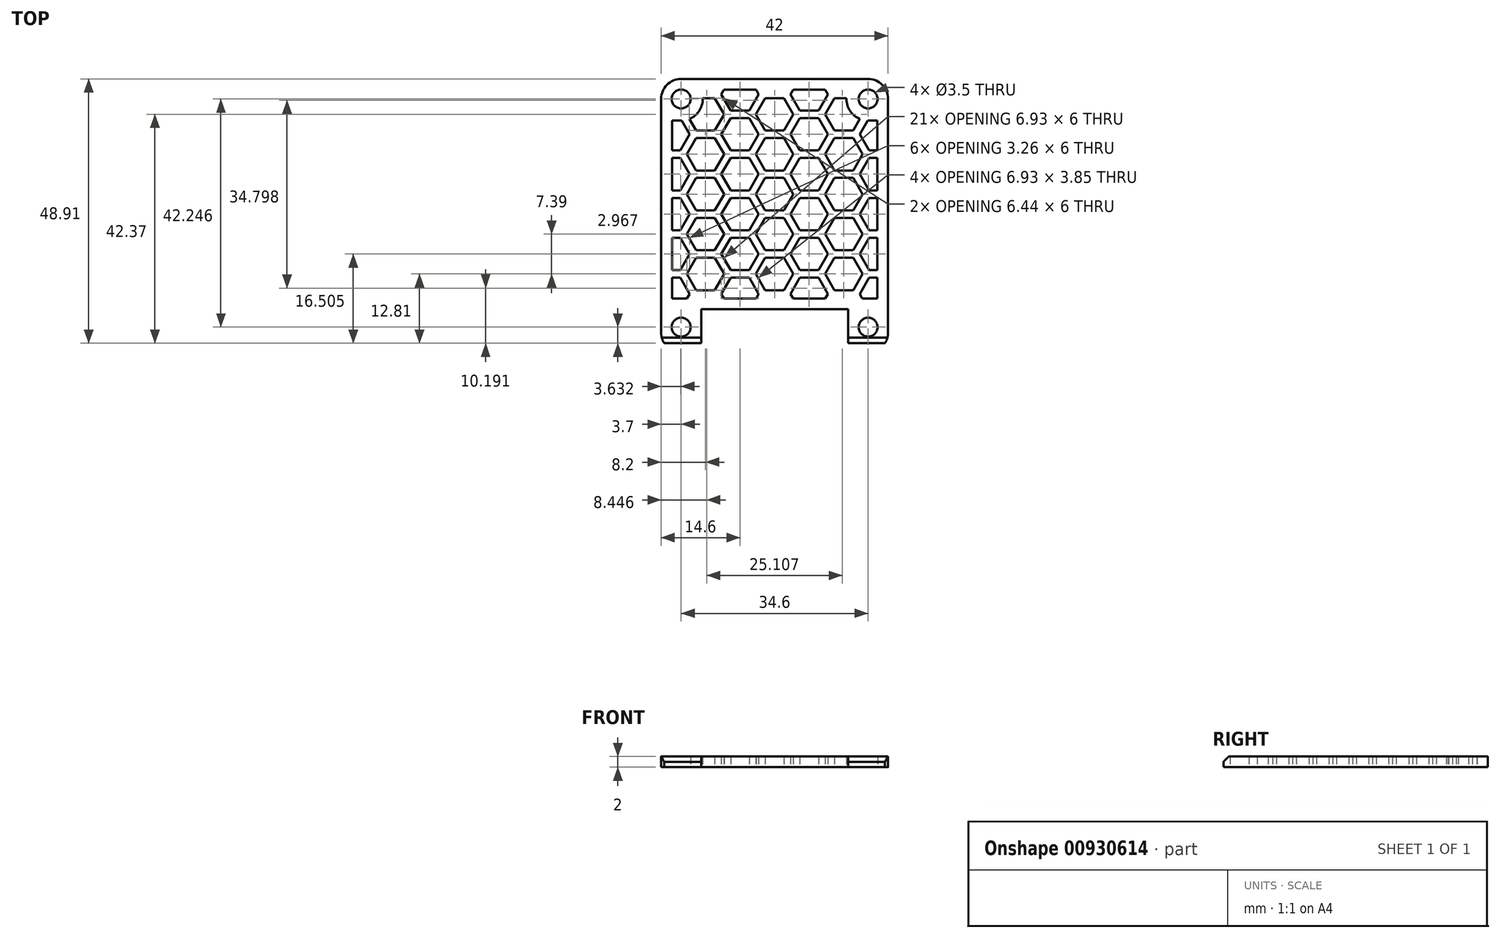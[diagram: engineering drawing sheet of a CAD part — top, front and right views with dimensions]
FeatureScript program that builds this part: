
annotation { "Feature Type Name" : "Feature", "Feature Type Description" : "" }
export const myFeature = defineFeature(function(context is Context, id is Id, definition is map)
    precondition{}
    {
        {
            var Q0;
            Q0=qCreatedBy(makeId("Top.planeOp"),FACE);
            var sketch = newSketch(context, id + "F0", { "sketchPlane" : qUnion([Q0])});
            skLineSegment(sketch, "E0", {"start": v(-21.3, 17.62) * mm, "end": v(-21.3, -25.62) * mm, "construction": true});
            skArc(sketch, "E1", {"start": v(-17.3, 21.62) * mm, "mid": v(-20.13, 20.45) * mm, "end": v(-21.3, 17.62) * mm, "construction": true});
            skLineSegment(sketch, "E2", {"start": v(-17.3, 21.62) * mm, "end": v(17.3, 21.62) * mm, "construction": true});
            skArc(sketch, "E3", {"start": v(21.3, 17.62) * mm, "mid": v(20.13, 20.45) * mm, "end": v(17.3, 21.62) * mm, "construction": true});
            skLineSegment(sketch, "E4", {"start": v(21.3, 17.62) * mm, "end": v(21.3, -25.62) * mm, "construction": true});
            skLineSegment(sketch, "E5", {"start": v(-13.3, -21.62) * mm, "end": v(13.3, -21.62) * mm, "construction": true});
            skLineSegment(sketch, "E6", {"start": v(13.3, -21.62) * mm, "end": v(13.3, -27.6) * mm, "construction": true});
            skLineSegment(sketch, "E7", {"start": v(-13.3, -21.62) * mm, "end": v(-13.3, -27.6) * mm, "construction": true});
            skArc(sketch, "E8", {"start": v(-21.3, -25.62) * mm, "mid": v(-21.17, -26.64) * mm, "end": v(-20.78, -27.6) * mm, "construction": true});
            skLineSegment(sketch, "E9", {"start": v(-20.78, -27.6) * mm, "end": v(-13.3, -27.6) * mm, "construction": true});
            skLineSegment(sketch, "E10", {"start": v(13.3, -27.6) * mm, "end": v(20.78, -27.6) * mm, "construction": true});
            skArc(sketch, "E11", {"start": v(20.78, -27.6) * mm, "mid": v(21.17, -26.64) * mm, "end": v(21.3, -25.62) * mm, "construction": true});
            skCircle(sketch, "E12", {"center": v(-17.3, 17.62) * mm, "radius": 1.4 * mm, "construction": true});
            skCircle(sketch, "E13", {"center": v(17.3, 17.62) * mm, "radius": 1.4 * mm, "construction": true});
            skCircle(sketch, "E14", {"center": v(-17.3, -24.62) * mm, "radius": 1.4 * mm, "construction": true});
            skCircle(sketch, "E15", {"center": v(17.3, -24.62) * mm, "radius": 1.4 * mm, "construction": true});
            skSolve(sketch);
        }
        {
            var Q0;
            Q0=qCreatedBy(makeId("Top.planeOp"),FACE);
            var sketch = newSketch(context, id + "F1", { "sketchPlane" : qUnion([Q0])});
            skLineSegment(sketch, "E16", {"start": v(-21, 17.62) * mm, "end": v(-21, -25.62) * mm});
            skLineSegment(sketch, "E17", {"start": v(-20.43, -27.6) * mm, "end": v(-13.6, -27.6) * mm});
            skLineSegment(sketch, "E18", {"start": v(-13.6, -27.6) * mm, "end": v(-13.6, -21.32) * mm});
            skArc(sketch, "E19", {"start": v(-21, -25.62) * mm, "mid": v(-20.85, -26.65) * mm, "end": v(-20.43, -27.6) * mm});
            skLineSegment(sketch, "E20", {"start": v(-17.3, 21.32) * mm, "end": v(17.3, 21.32) * mm});
            skLineSegment(sketch, "E21", {"start": v(21, 17.62) * mm, "end": v(21, -25.62) * mm});
            skLineSegment(sketch, "E22", {"start": v(-13.6, -21.32) * mm, "end": v(13.6, -21.32) * mm});
            skLineSegment(sketch, "E23", {"start": v(13.6, -21.32) * mm, "end": v(13.6, -27.6) * mm});
            skLineSegment(sketch, "E24", {"start": v(13.6, -27.6) * mm, "end": v(20.43, -27.6) * mm});
            skArc(sketch, "E25", {"start": v(20.43, -27.6) * mm, "mid": v(20.85, -26.65) * mm, "end": v(21, -25.62) * mm});
            skArc(sketch, "E26", {"start": v(21, 17.62) * mm, "mid": v(19.92, 20.24) * mm, "end": v(17.3, 21.32) * mm});
            skArc(sketch, "E27", {"start": v(-17.3, 21.32) * mm, "mid": v(-19.92, 20.24) * mm, "end": v(-21, 17.62) * mm});
            skCircle(sketch, "E28", {"center": v(-17.3, 17.62) * mm, "radius": 1.75 * mm});
            skCircle(sketch, "E29", {"center": v(17.3, 17.62) * mm, "radius": 1.75 * mm});
            skCircle(sketch, "E30", {"center": v(-17.3, -24.62) * mm, "radius": 1.75 * mm});
            skCircle(sketch, "E31", {"center": v(17.3, -24.62) * mm, "radius": 1.75 * mm});
            skLineSegment(sketch, "E32", {"start": v(-9.37, 19.32) * mm, "end": v(-3.43, 19.32) * mm});
            skLineSegment(sketch, "E33", {"start": v(13.3, 17.78) * mm, "end": v(13.3, 17.62) * mm});
            skLineSegment(sketch, "E34", {"start": v(-13.3, 17.78) * mm, "end": v(-13.3, 17.62) * mm});
            skLineSegment(sketch, "E35", {"start": v(-19, -19.32) * mm, "end": v(-16.23, -19.32) * mm});
            skLineSegment(sketch, "E36", {"start": v(19, -19.32) * mm, "end": v(19, -15.48) * mm});
            skLineSegment(sketch, "E37", {"start": v(19, 13.62) * mm, "end": v(17.3, 13.62) * mm});
            skLineSegment(sketch, "E38", {"start": v(-19, -19.32) * mm, "end": v(-19, -15.48) * mm});
            skLineSegment(sketch, "E39", {"start": v(-19, 13.62) * mm, "end": v(-17.3, 13.62) * mm});
            skArc(sketch, "E40", {"start": v(-17.3, 13.62) * mm, "mid": v(-17.25, 13.62) * mm, "end": v(-17.2, 13.62) * mm});
            skArc(sketch, "E41", {"start": v(13.3, 17.62) * mm, "mid": v(13.97, 15.4) * mm, "end": v(15.77, 13.93) * mm});
            skCircle(sketch, "E42.cCircle", {"center": v(0, 0) * mm, "radius": 3 * mm, "construction": true});
            skLineSegment(sketch, "E42.0", {"start": v(1.73, 3) * mm, "end": v(3.46, 0) * mm});
            skLineSegment(sketch, "E42.1", {"start": v(3.46, 0) * mm, "end": v(1.73, -3) * mm});
            skLineSegment(sketch, "E42.2", {"start": v(1.73, -3) * mm, "end": v(-1.73, -3) * mm});
            skLineSegment(sketch, "E42.3", {"start": v(-1.73, -3) * mm, "end": v(-3.46, 0) * mm});
            skLineSegment(sketch, "E42.4", {"start": v(-3.46, 0) * mm, "end": v(-1.73, 3) * mm});
            skLineSegment(sketch, "E42.5", {"start": v(-1.73, 3) * mm, "end": v(1.73, 3) * mm});
            skPoint(sketch, "E42.0.midPoint", {"position": v(2.6, 1.5) * mm});
            skLineSegment(sketch, "E43", {"start": v(-19, 10.97) * mm, "end": v(19, -10.97) * mm, "construction": true});
            skLineSegment(sketch, "E44", {"start": v(-19, -10.97) * mm, "end": v(19, 10.97) * mm, "construction": true});
            skLineSegment(sketch, "E45", {"start": v(-13.95, 15.44) * mm, "end": v(19, -3.58) * mm, "construction": true});
            skCircle(sketch, "E46.cCircle", {"center": v(6.4, 3.7) * mm, "radius": 3 * mm, "construction": true});
            skLineSegment(sketch, "E46.0", {"start": v(8.13, 6.7) * mm, "end": v(9.86, 3.7) * mm});
            skLineSegment(sketch, "E46.1", {"start": v(9.86, 3.7) * mm, "end": v(8.13, 0.7) * mm});
            skLineSegment(sketch, "E46.2", {"start": v(8.13, 0.7) * mm, "end": v(4.67, 0.7) * mm});
            skLineSegment(sketch, "E46.3", {"start": v(4.67, 0.7) * mm, "end": v(2.94, 3.7) * mm});
            skLineSegment(sketch, "E46.4", {"start": v(2.94, 3.7) * mm, "end": v(4.67, 6.7) * mm});
            skLineSegment(sketch, "E46.5", {"start": v(4.67, 6.7) * mm, "end": v(8.13, 6.7) * mm});
            skPoint(sketch, "E46.0.midPoint", {"position": v(9, 5.2) * mm});
            skLineSegment(sketch, "E47", {"start": v(-19, 3.58) * mm, "end": v(19, -18.36) * mm, "construction": true});
            skLineSegment(sketch, "E48", {"start": v(-19, -3.81) * mm, "end": v(7.87, -19.32) * mm, "construction": true});
            skLineSegment(sketch, "E49", {"start": v(-19, -11.2) * mm, "end": v(-4.93, -19.32) * mm, "construction": true});
            skLineSegment(sketch, "E50", {"start": v(-19, -18.6) * mm, "end": v(-17.73, -19.32) * mm, "construction": true});
            skLineSegment(sketch, "E51", {"start": v(-7.87, 19.32) * mm, "end": v(19, 3.81) * mm, "construction": true});
            skLineSegment(sketch, "E52", {"start": v(4.93, 19.32) * mm, "end": v(19, 11.2) * mm, "construction": true});
            skLineSegment(sketch, "E53", {"start": v(-19, -3.58) * mm, "end": v(13.95, 15.44) * mm, "construction": true});
            skLineSegment(sketch, "E54", {"start": v(-19, 3.81) * mm, "end": v(7.87, 19.32) * mm, "construction": true});
            skLineSegment(sketch, "E55", {"start": v(-19, 11.2) * mm, "end": v(-4.93, 19.32) * mm, "construction": true});
            skLineSegment(sketch, "E56", {"start": v(-19, -18.36) * mm, "end": v(19, 3.58) * mm, "construction": true});
            skLineSegment(sketch, "E57", {"start": v(-7.87, -19.32) * mm, "end": v(19, -3.81) * mm, "construction": true});
            skLineSegment(sketch, "E58", {"start": v(4.93, -19.32) * mm, "end": v(19, -11.2) * mm, "construction": true});
            skLineSegment(sketch, "E59", {"start": v(17.73, -19.32) * mm, "end": v(19, -18.6) * mm, "construction": true});
            skCircle(sketch, "E60.cCircle", {"center": v(0, -7.4) * mm, "radius": 3 * mm, "construction": true});
            skLineSegment(sketch, "E60.0", {"start": v(1.73, -4.4) * mm, "end": v(3.46, -7.4) * mm});
            skLineSegment(sketch, "E60.1", {"start": v(3.46, -7.4) * mm, "end": v(1.73, -10.4) * mm});
            skLineSegment(sketch, "E60.2", {"start": v(1.73, -10.4) * mm, "end": v(-1.73, -10.4) * mm});
            skLineSegment(sketch, "E60.3", {"start": v(-1.73, -10.4) * mm, "end": v(-3.46, -7.4) * mm});
            skLineSegment(sketch, "E60.4", {"start": v(-3.46, -7.4) * mm, "end": v(-1.73, -4.4) * mm});
            skLineSegment(sketch, "E60.5", {"start": v(-1.73, -4.4) * mm, "end": v(1.73, -4.4) * mm});
            skPoint(sketch, "E60.0.midPoint", {"position": v(2.6, -5.9) * mm});
            skCircle(sketch, "E61.cCircle", {"center": v(6.4, -3.7) * mm, "radius": 3 * mm, "construction": true});
            skLineSegment(sketch, "E61.0", {"start": v(8.13, -0.7) * mm, "end": v(9.86, -3.7) * mm});
            skLineSegment(sketch, "E61.1", {"start": v(9.86, -3.7) * mm, "end": v(8.13, -6.7) * mm});
            skLineSegment(sketch, "E61.2", {"start": v(8.13, -6.7) * mm, "end": v(4.67, -6.7) * mm});
            skLineSegment(sketch, "E61.3", {"start": v(4.67, -6.7) * mm, "end": v(2.94, -3.7) * mm});
            skLineSegment(sketch, "E61.4", {"start": v(2.94, -3.7) * mm, "end": v(4.67, -0.7) * mm});
            skLineSegment(sketch, "E61.5", {"start": v(4.67, -0.7) * mm, "end": v(8.13, -0.7) * mm});
            skPoint(sketch, "E61.0.midPoint", {"position": v(9, -2.2) * mm});
            skCircle(sketch, "E62.cCircle", {"center": v(6.4, -11.09) * mm, "radius": 3 * mm, "construction": true});
            skLineSegment(sketch, "E62.0", {"start": v(8.13, -8.09) * mm, "end": v(9.86, -11.09) * mm});
            skLineSegment(sketch, "E62.1", {"start": v(9.86, -11.09) * mm, "end": v(8.13, -14.09) * mm});
            skLineSegment(sketch, "E62.2", {"start": v(8.13, -14.09) * mm, "end": v(4.67, -14.09) * mm});
            skLineSegment(sketch, "E62.3", {"start": v(4.67, -14.09) * mm, "end": v(2.94, -11.09) * mm});
            skLineSegment(sketch, "E62.4", {"start": v(2.94, -11.09) * mm, "end": v(4.67, -8.09) * mm});
            skLineSegment(sketch, "E62.5", {"start": v(4.67, -8.09) * mm, "end": v(8.13, -8.09) * mm});
            skPoint(sketch, "E62.0.midPoint", {"position": v(9, -9.59) * mm});
            skCircle(sketch, "E63.cCircle", {"center": v(0, -14.78) * mm, "radius": 3 * mm, "construction": true});
            skLineSegment(sketch, "E63.0", {"start": v(1.73, -11.78) * mm, "end": v(3.46, -14.78) * mm});
            skLineSegment(sketch, "E63.1", {"start": v(3.46, -14.78) * mm, "end": v(1.73, -17.78) * mm});
            skLineSegment(sketch, "E63.2", {"start": v(1.73, -17.78) * mm, "end": v(-1.73, -17.78) * mm});
            skLineSegment(sketch, "E63.3", {"start": v(-1.73, -17.78) * mm, "end": v(-3.46, -14.78) * mm});
            skLineSegment(sketch, "E63.4", {"start": v(-3.46, -14.78) * mm, "end": v(-1.73, -11.78) * mm});
            skLineSegment(sketch, "E63.5", {"start": v(-1.73, -11.78) * mm, "end": v(1.73, -11.78) * mm});
            skPoint(sketch, "E63.0.midPoint", {"position": v(2.6, -13.28) * mm});
            skCircle(sketch, "E64.cCircle", {"center": v(12.8, -7.4) * mm, "radius": 3 * mm, "construction": true});
            skLineSegment(sketch, "E64.0", {"start": v(14.53, -4.4) * mm, "end": v(16.26, -7.4) * mm});
            skLineSegment(sketch, "E64.1", {"start": v(16.26, -7.4) * mm, "end": v(14.53, -10.4) * mm});
            skLineSegment(sketch, "E64.2", {"start": v(14.53, -10.4) * mm, "end": v(11.07, -10.4) * mm});
            skLineSegment(sketch, "E64.3", {"start": v(11.07, -10.4) * mm, "end": v(9.34, -7.4) * mm});
            skLineSegment(sketch, "E64.4", {"start": v(9.34, -7.4) * mm, "end": v(11.07, -4.4) * mm});
            skLineSegment(sketch, "E64.5", {"start": v(11.07, -4.4) * mm, "end": v(14.53, -4.4) * mm});
            skPoint(sketch, "E64.0.midPoint", {"position": v(15.4, -5.9) * mm});
            skCircle(sketch, "E65.cCircle", {"center": v(12.8, 0) * mm, "radius": 3 * mm, "construction": true});
            skLineSegment(sketch, "E65.0", {"start": v(14.53, 3) * mm, "end": v(16.26, 0) * mm});
            skLineSegment(sketch, "E65.1", {"start": v(16.26, 0) * mm, "end": v(14.53, -3) * mm});
            skLineSegment(sketch, "E65.2", {"start": v(14.53, -3) * mm, "end": v(11.07, -3) * mm});
            skLineSegment(sketch, "E65.3", {"start": v(11.07, -3) * mm, "end": v(9.34, 0) * mm});
            skLineSegment(sketch, "E65.4", {"start": v(9.34, 0) * mm, "end": v(11.07, 3) * mm});
            skLineSegment(sketch, "E65.5", {"start": v(11.07, 3) * mm, "end": v(14.53, 3) * mm});
            skPoint(sketch, "E65.0.midPoint", {"position": v(15.4, 1.5) * mm});
            skCircle(sketch, "E66.cCircle", {"center": v(12.8, 7.4) * mm, "radius": 3 * mm, "construction": true});
            skLineSegment(sketch, "E66.0", {"start": v(14.53, 10.4) * mm, "end": v(16.26, 7.4) * mm});
            skLineSegment(sketch, "E66.1", {"start": v(16.26, 7.4) * mm, "end": v(14.53, 4.4) * mm});
            skLineSegment(sketch, "E66.2", {"start": v(14.53, 4.4) * mm, "end": v(11.07, 4.4) * mm});
            skLineSegment(sketch, "E66.3", {"start": v(11.07, 4.4) * mm, "end": v(9.34, 7.4) * mm});
            skLineSegment(sketch, "E66.4", {"start": v(9.34, 7.4) * mm, "end": v(11.07, 10.4) * mm});
            skLineSegment(sketch, "E66.5", {"start": v(11.07, 10.4) * mm, "end": v(14.53, 10.4) * mm});
            skPoint(sketch, "E66.0.midPoint", {"position": v(15.4, 8.9) * mm});
            skCircle(sketch, "E67.cCircle", {"center": v(12.8, -14.78) * mm, "radius": 3 * mm, "construction": true});
            skLineSegment(sketch, "E67.0", {"start": v(14.53, -11.78) * mm, "end": v(16.26, -14.78) * mm});
            skLineSegment(sketch, "E67.1", {"start": v(16.26, -14.78) * mm, "end": v(14.53, -17.78) * mm});
            skLineSegment(sketch, "E67.2", {"start": v(14.53, -17.78) * mm, "end": v(11.07, -17.78) * mm});
            skLineSegment(sketch, "E67.3", {"start": v(11.07, -17.78) * mm, "end": v(9.34, -14.78) * mm});
            skLineSegment(sketch, "E67.4", {"start": v(9.34, -14.78) * mm, "end": v(11.07, -11.78) * mm});
            skLineSegment(sketch, "E67.5", {"start": v(11.07, -11.78) * mm, "end": v(14.53, -11.78) * mm});
            skPoint(sketch, "E67.0.midPoint", {"position": v(15.4, -13.28) * mm});
            skArc(sketch, "E68.cCircle", {"start": v(9.28, -19.32) * mm, "mid": v(6.4, -15.48) * mm, "end": v(3.52, -19.32) * mm, "construction": true});
            skLineSegment(sketch, "E68.0", {"start": v(8.13, -15.48) * mm, "end": v(9.86, -18.48) * mm});
            skLineSegment(sketch, "E68.1", {"start": v(9.86, -18.48) * mm, "end": v(9.37, -19.32) * mm});
            skLineSegment(sketch, "E68.4", {"start": v(2.94, -18.48) * mm, "end": v(4.67, -15.48) * mm});
            skLineSegment(sketch, "E68.5", {"start": v(4.67, -15.48) * mm, "end": v(8.13, -15.48) * mm});
            skPoint(sketch, "E68.0.midPoint", {"position": v(9, -16.98) * mm});
            skCircle(sketch, "E69.cCircle", {"center": v(6.4, 11.09) * mm, "radius": 3 * mm, "construction": true});
            skLineSegment(sketch, "E69.0", {"start": v(8.13, 14.09) * mm, "end": v(9.86, 11.09) * mm});
            skLineSegment(sketch, "E69.1", {"start": v(9.86, 11.09) * mm, "end": v(8.13, 8.09) * mm});
            skLineSegment(sketch, "E69.2", {"start": v(8.13, 8.09) * mm, "end": v(4.67, 8.09) * mm});
            skLineSegment(sketch, "E69.3", {"start": v(4.67, 8.09) * mm, "end": v(2.94, 11.09) * mm});
            skLineSegment(sketch, "E69.4", {"start": v(2.94, 11.09) * mm, "end": v(4.67, 14.09) * mm});
            skLineSegment(sketch, "E69.5", {"start": v(4.67, 14.09) * mm, "end": v(8.13, 14.09) * mm});
            skPoint(sketch, "E69.0.midPoint", {"position": v(9, 12.59) * mm});
            skCircle(sketch, "E70.cCircle", {"center": v(0, 7.4) * mm, "radius": 3 * mm, "construction": true});
            skLineSegment(sketch, "E70.0", {"start": v(-3.46, 7.4) * mm, "end": v(-1.73, 10.4) * mm});
            skLineSegment(sketch, "E70.1", {"start": v(-1.73, 10.4) * mm, "end": v(1.73, 10.4) * mm});
            skLineSegment(sketch, "E70.2", {"start": v(1.73, 10.4) * mm, "end": v(3.46, 7.4) * mm});
            skLineSegment(sketch, "E70.3", {"start": v(3.46, 7.4) * mm, "end": v(1.73, 4.4) * mm});
            skLineSegment(sketch, "E70.4", {"start": v(1.73, 4.4) * mm, "end": v(-1.73, 4.4) * mm});
            skLineSegment(sketch, "E70.5", {"start": v(-1.73, 4.4) * mm, "end": v(-3.46, 7.4) * mm});
            skPoint(sketch, "E70.0.midPoint", {"position": v(-2.6, 8.9) * mm});
            skCircle(sketch, "E71.cCircle", {"center": v(0, 14.78) * mm, "radius": 3 * mm, "construction": true});
            skLineSegment(sketch, "E71.0", {"start": v(1.73, 17.78) * mm, "end": v(3.46, 14.78) * mm});
            skLineSegment(sketch, "E71.1", {"start": v(3.46, 14.78) * mm, "end": v(1.73, 11.78) * mm});
            skLineSegment(sketch, "E71.2", {"start": v(1.73, 11.78) * mm, "end": v(-1.73, 11.78) * mm});
            skLineSegment(sketch, "E71.3", {"start": v(-1.73, 11.78) * mm, "end": v(-3.46, 14.78) * mm});
            skLineSegment(sketch, "E71.4", {"start": v(-3.46, 14.78) * mm, "end": v(-1.73, 17.78) * mm});
            skLineSegment(sketch, "E71.5", {"start": v(-1.73, 17.78) * mm, "end": v(1.73, 17.78) * mm});
            skPoint(sketch, "E71.0.midPoint", {"position": v(2.6, 16.28) * mm});
            skArc(sketch, "E72.cCircle", {"start": v(3.52, 19.32) * mm, "mid": v(6.4, 15.48) * mm, "end": v(9.28, 19.32) * mm, "construction": true});
            skLineSegment(sketch, "E72.0", {"start": v(4.67, 15.48) * mm, "end": v(2.94, 18.48) * mm});
            skLineSegment(sketch, "E72.1", {"start": v(2.94, 18.48) * mm, "end": v(3.43, 19.32) * mm});
            skLineSegment(sketch, "E72.3", {"start": v(9.37, 19.32) * mm, "end": v(9.86, 18.48) * mm});
            skLineSegment(sketch, "E72.4", {"start": v(9.86, 18.48) * mm, "end": v(8.13, 15.48) * mm});
            skLineSegment(sketch, "E72.5", {"start": v(8.13, 15.48) * mm, "end": v(4.67, 15.48) * mm});
            skPoint(sketch, "E72.0.midPoint", {"position": v(3.8, 16.98) * mm});
            skArc(sketch, "E73.cCircle", {"start": v(13.3, 17.74) * mm, "mid": v(10.26, 13.18) * mm, "end": v(15.69, 13.96) * mm, "construction": true});
            skLineSegment(sketch, "E73.0", {"start": v(9.34, 14.78) * mm, "end": v(11.07, 17.78) * mm});
            skLineSegment(sketch, "E73.1", {"start": v(11.07, 17.78) * mm, "end": v(13.3, 17.78) * mm});
            skLineSegment(sketch, "E73.3", {"start": v(15.77, 13.93) * mm, "end": v(14.53, 11.78) * mm});
            skLineSegment(sketch, "E73.4", {"start": v(14.53, 11.78) * mm, "end": v(11.07, 11.78) * mm});
            skLineSegment(sketch, "E73.5", {"start": v(11.07, 11.78) * mm, "end": v(9.34, 14.78) * mm});
            skPoint(sketch, "E73.0.midPoint", {"position": v(10.2, 16.28) * mm});
            skLineSegment(sketch, "E74.trimOffspring", {"start": v(3.43, -19.32) * mm, "end": v(2.94, -18.48) * mm});
            skPoint(sketch, "E75.orphan", {"position": v(8.13, 21.48) * mm});
            skArc(sketch, "E76.cCircle", {"start": v(17.6, 13.62) * mm, "mid": v(16.3, 10.35) * mm, "end": v(19, 8.1) * mm, "construction": true});
            skLineSegment(sketch, "E76.3", {"start": v(19, 8.09) * mm, "end": v(17.47, 8.09) * mm});
            skLineSegment(sketch, "E76.4", {"start": v(17.47, 8.09) * mm, "end": v(15.74, 11.09) * mm});
            skLineSegment(sketch, "E76.5", {"start": v(15.74, 11.09) * mm, "end": v(17.2, 13.62) * mm});
            skPoint(sketch, "E77.orphan", {"position": v(17.47, 14.09) * mm});
            skPoint(sketch, "E78.orphan", {"position": v(14.53, 17.78) * mm});
            skPoint(sketch, "E79.orphan", {"position": v(16.26, 14.78) * mm});
            skArc(sketch, "E80.trimOffspring", {"start": v(17.2, 13.62) * mm, "mid": v(17.25, 13.62) * mm, "end": v(17.3, 13.62) * mm});
            skCircle(sketch, "E81.cCircle", {"center": v(-6.4, 11.09) * mm, "radius": 3 * mm, "construction": true});
            skLineSegment(sketch, "E81.0", {"start": v(-4.67, 14.09) * mm, "end": v(-2.94, 11.09) * mm});
            skLineSegment(sketch, "E81.1", {"start": v(-2.94, 11.09) * mm, "end": v(-4.67, 8.09) * mm});
            skLineSegment(sketch, "E81.2", {"start": v(-4.67, 8.09) * mm, "end": v(-8.13, 8.09) * mm});
            skLineSegment(sketch, "E81.3", {"start": v(-8.13, 8.09) * mm, "end": v(-9.86, 11.09) * mm});
            skLineSegment(sketch, "E81.4", {"start": v(-9.86, 11.09) * mm, "end": v(-8.13, 14.09) * mm});
            skLineSegment(sketch, "E81.5", {"start": v(-8.13, 14.09) * mm, "end": v(-4.67, 14.09) * mm});
            skPoint(sketch, "E81.0.midPoint", {"position": v(-3.8, 12.59) * mm});
            skCircle(sketch, "E82.cCircle", {"center": v(-6.4, 3.7) * mm, "radius": 3 * mm, "construction": true});
            skLineSegment(sketch, "E82.0", {"start": v(-4.67, 6.7) * mm, "end": v(-2.94, 3.7) * mm});
            skLineSegment(sketch, "E82.1", {"start": v(-2.94, 3.7) * mm, "end": v(-4.67, 0.7) * mm});
            skLineSegment(sketch, "E82.2", {"start": v(-4.67, 0.7) * mm, "end": v(-8.13, 0.7) * mm});
            skLineSegment(sketch, "E82.3", {"start": v(-8.13, 0.7) * mm, "end": v(-9.86, 3.7) * mm});
            skLineSegment(sketch, "E82.4", {"start": v(-9.86, 3.7) * mm, "end": v(-8.13, 6.7) * mm});
            skLineSegment(sketch, "E82.5", {"start": v(-8.13, 6.7) * mm, "end": v(-4.67, 6.7) * mm});
            skPoint(sketch, "E82.0.midPoint", {"position": v(-3.8, 5.2) * mm});
            skCircle(sketch, "E83.cCircle", {"center": v(-6.4, -3.7) * mm, "radius": 3 * mm, "construction": true});
            skLineSegment(sketch, "E83.0", {"start": v(-4.67, -0.7) * mm, "end": v(-2.94, -3.7) * mm});
            skLineSegment(sketch, "E83.1", {"start": v(-2.94, -3.7) * mm, "end": v(-4.67, -6.7) * mm});
            skLineSegment(sketch, "E83.2", {"start": v(-4.67, -6.7) * mm, "end": v(-8.13, -6.7) * mm});
            skLineSegment(sketch, "E83.3", {"start": v(-8.13, -6.7) * mm, "end": v(-9.86, -3.7) * mm});
            skLineSegment(sketch, "E83.4", {"start": v(-9.86, -3.7) * mm, "end": v(-8.13, -0.7) * mm});
            skLineSegment(sketch, "E83.5", {"start": v(-8.13, -0.7) * mm, "end": v(-4.67, -0.7) * mm});
            skPoint(sketch, "E83.0.midPoint", {"position": v(-3.8, -2.2) * mm});
            skCircle(sketch, "E84.cCircle", {"center": v(-6.4, -11.09) * mm, "radius": 3 * mm, "construction": true});
            skLineSegment(sketch, "E84.0", {"start": v(-4.67, -8.09) * mm, "end": v(-2.94, -11.09) * mm});
            skLineSegment(sketch, "E84.1", {"start": v(-2.94, -11.09) * mm, "end": v(-4.67, -14.09) * mm});
            skLineSegment(sketch, "E84.2", {"start": v(-4.67, -14.09) * mm, "end": v(-8.13, -14.09) * mm});
            skLineSegment(sketch, "E84.3", {"start": v(-8.13, -14.09) * mm, "end": v(-9.86, -11.09) * mm});
            skLineSegment(sketch, "E84.4", {"start": v(-9.86, -11.09) * mm, "end": v(-8.13, -8.09) * mm});
            skLineSegment(sketch, "E84.5", {"start": v(-8.13, -8.09) * mm, "end": v(-4.67, -8.09) * mm});
            skPoint(sketch, "E84.0.midPoint", {"position": v(-3.8, -9.59) * mm});
            skCircle(sketch, "E85.cCircle", {"center": v(-12.8, 7.4) * mm, "radius": 3 * mm, "construction": true});
            skLineSegment(sketch, "E85.0", {"start": v(-11.07, 10.4) * mm, "end": v(-9.34, 7.4) * mm});
            skLineSegment(sketch, "E85.1", {"start": v(-9.34, 7.4) * mm, "end": v(-11.07, 4.4) * mm});
            skLineSegment(sketch, "E85.2", {"start": v(-11.07, 4.4) * mm, "end": v(-14.53, 4.4) * mm});
            skLineSegment(sketch, "E85.3", {"start": v(-14.53, 4.4) * mm, "end": v(-16.26, 7.4) * mm});
            skLineSegment(sketch, "E85.4", {"start": v(-16.26, 7.4) * mm, "end": v(-14.53, 10.4) * mm});
            skLineSegment(sketch, "E85.5", {"start": v(-14.53, 10.4) * mm, "end": v(-11.07, 10.4) * mm});
            skPoint(sketch, "E85.0.midPoint", {"position": v(-10.2, 8.9) * mm});
            skCircle(sketch, "E86.cCircle", {"center": v(-12.8, 0) * mm, "radius": 3 * mm, "construction": true});
            skLineSegment(sketch, "E86.0", {"start": v(-11.07, 3) * mm, "end": v(-9.34, 0) * mm});
            skLineSegment(sketch, "E86.1", {"start": v(-9.34, 0) * mm, "end": v(-11.07, -3) * mm});
            skLineSegment(sketch, "E86.2", {"start": v(-11.07, -3) * mm, "end": v(-14.53, -3) * mm});
            skLineSegment(sketch, "E86.3", {"start": v(-14.53, -3) * mm, "end": v(-16.26, 0) * mm});
            skLineSegment(sketch, "E86.4", {"start": v(-16.26, 0) * mm, "end": v(-14.53, 3) * mm});
            skLineSegment(sketch, "E86.5", {"start": v(-14.53, 3) * mm, "end": v(-11.07, 3) * mm});
            skPoint(sketch, "E86.0.midPoint", {"position": v(-10.2, 1.5) * mm});
            skCircle(sketch, "E87.cCircle", {"center": v(-12.8, -7.4) * mm, "radius": 3 * mm, "construction": true});
            skLineSegment(sketch, "E87.0", {"start": v(-11.07, -4.4) * mm, "end": v(-9.34, -7.4) * mm});
            skLineSegment(sketch, "E87.1", {"start": v(-9.34, -7.4) * mm, "end": v(-11.07, -10.4) * mm});
            skLineSegment(sketch, "E87.2", {"start": v(-11.07, -10.4) * mm, "end": v(-14.53, -10.4) * mm});
            skLineSegment(sketch, "E87.3", {"start": v(-14.53, -10.4) * mm, "end": v(-16.26, -7.4) * mm});
            skLineSegment(sketch, "E87.4", {"start": v(-16.26, -7.4) * mm, "end": v(-14.53, -4.4) * mm});
            skLineSegment(sketch, "E87.5", {"start": v(-14.53, -4.4) * mm, "end": v(-11.07, -4.4) * mm});
            skPoint(sketch, "E87.0.midPoint", {"position": v(-10.2, -5.9) * mm});
            skCircle(sketch, "E88.cCircle", {"center": v(-12.8, -14.78) * mm, "radius": 3 * mm, "construction": true});
            skLineSegment(sketch, "E88.0", {"start": v(-11.07, -11.78) * mm, "end": v(-9.34, -14.78) * mm});
            skLineSegment(sketch, "E88.1", {"start": v(-9.34, -14.78) * mm, "end": v(-11.07, -17.78) * mm});
            skLineSegment(sketch, "E88.2", {"start": v(-11.07, -17.78) * mm, "end": v(-14.53, -17.78) * mm});
            skLineSegment(sketch, "E88.3", {"start": v(-14.53, -17.78) * mm, "end": v(-16.26, -14.78) * mm});
            skLineSegment(sketch, "E88.4", {"start": v(-16.26, -14.78) * mm, "end": v(-14.53, -11.78) * mm});
            skLineSegment(sketch, "E88.5", {"start": v(-14.53, -11.78) * mm, "end": v(-11.07, -11.78) * mm});
            skPoint(sketch, "E88.0.midPoint", {"position": v(-10.2, -13.28) * mm});
            skArc(sketch, "E89.cCircle", {"start": v(-9.28, 19.32) * mm, "mid": v(-6.4, 15.48) * mm, "end": v(-3.52, 19.32) * mm, "construction": true});
            skLineSegment(sketch, "E89.0", {"start": v(-2.94, 18.48) * mm, "end": v(-4.67, 15.48) * mm});
            skLineSegment(sketch, "E89.1", {"start": v(-4.67, 15.48) * mm, "end": v(-8.13, 15.48) * mm});
            skLineSegment(sketch, "E89.2", {"start": v(-8.13, 15.48) * mm, "end": v(-9.86, 18.48) * mm});
            skLineSegment(sketch, "E89.3", {"start": v(-9.86, 18.48) * mm, "end": v(-9.37, 19.32) * mm});
            skLineSegment(sketch, "E89.5", {"start": v(-3.43, 19.32) * mm, "end": v(-2.94, 18.48) * mm});
            skPoint(sketch, "E89.0.midPoint", {"position": v(-3.8, 16.98) * mm});
            skArc(sketch, "E90.cCircle", {"start": v(-15.69, 13.96) * mm, "mid": v(-10.26, 13.18) * mm, "end": v(-13.3, 17.74) * mm, "construction": true});
            skLineSegment(sketch, "E90.0", {"start": v(-9.34, 14.78) * mm, "end": v(-11.07, 11.78) * mm});
            skLineSegment(sketch, "E90.1", {"start": v(-11.07, 11.78) * mm, "end": v(-14.53, 11.78) * mm});
            skLineSegment(sketch, "E90.2", {"start": v(-14.53, 11.78) * mm, "end": v(-15.77, 13.93) * mm});
            skLineSegment(sketch, "E90.4", {"start": v(-13.3, 17.78) * mm, "end": v(-11.07, 17.78) * mm});
            skLineSegment(sketch, "E90.5", {"start": v(-11.07, 17.78) * mm, "end": v(-9.34, 14.78) * mm});
            skPoint(sketch, "E90.0.midPoint", {"position": v(-10.2, 13.28) * mm});
            skArc(sketch, "E91.cCircle", {"start": v(-3.52, -19.32) * mm, "mid": v(-6.4, -15.48) * mm, "end": v(-9.28, -19.32) * mm, "construction": true});
            skPoint(sketch, "E91.cCircle.centerSnap0", {"position": v(-6.4, -14.09) * mm});
            skLineSegment(sketch, "E91.0", {"start": v(-4.67, -15.48) * mm, "end": v(-2.94, -18.48) * mm});
            skLineSegment(sketch, "E91.1", {"start": v(-2.94, -18.48) * mm, "end": v(-3.43, -19.32) * mm});
            skLineSegment(sketch, "E91.3", {"start": v(-9.37, -19.32) * mm, "end": v(-9.86, -18.48) * mm});
            skLineSegment(sketch, "E91.4", {"start": v(-9.86, -18.48) * mm, "end": v(-8.13, -15.48) * mm});
            skLineSegment(sketch, "E91.5", {"start": v(-8.13, -15.48) * mm, "end": v(-4.67, -15.48) * mm});
            skPoint(sketch, "E91.0.midPoint", {"position": v(-3.8, -16.98) * mm});
            skPoint(sketch, "E92.orphan", {"position": v(-4.67, 21.48) * mm});
            skLineSegment(sketch, "E93.trimOffspring", {"start": v(3.43, 19.32) * mm, "end": v(9.37, 19.32) * mm});
            skPoint(sketch, "E94.orphan", {"position": v(-14.53, 17.78) * mm});
            skArc(sketch, "E95.cCircle", {"start": v(-19, 8.1) * mm, "mid": v(-16.3, 10.35) * mm, "end": v(-17.6, 13.62) * mm, "construction": true});
            skLineSegment(sketch, "E95.1", {"start": v(-17.2, 13.62) * mm, "end": v(-15.74, 11.09) * mm});
            skLineSegment(sketch, "E95.2", {"start": v(-15.74, 11.09) * mm, "end": v(-17.47, 8.09) * mm});
            skLineSegment(sketch, "E95.3", {"start": v(-17.47, 8.09) * mm, "end": v(-19, 8.09) * mm});
            skPoint(sketch, "E95.0.midPoint", {"position": v(-19.2, 14.09) * mm});
            skArc(sketch, "E96.cCircle", {"start": v(-19, 0.7) * mm, "mid": v(-16.2, 3.7) * mm, "end": v(-19, 6.69) * mm, "construction": true});
            skLineSegment(sketch, "E96.1", {"start": v(-19, 6.7) * mm, "end": v(-17.47, 6.7) * mm});
            skLineSegment(sketch, "E96.2", {"start": v(-17.47, 6.7) * mm, "end": v(-15.74, 3.7) * mm});
            skLineSegment(sketch, "E96.3", {"start": v(-15.74, 3.7) * mm, "end": v(-17.47, 0.7) * mm});
            skLineSegment(sketch, "E96.4", {"start": v(-17.47, 0.7) * mm, "end": v(-19, 0.7) * mm});
            skArc(sketch, "E97.cCircle", {"start": v(-19, -6.69) * mm, "mid": v(-16.2, -3.7) * mm, "end": v(-19, -0.7) * mm, "construction": true});
            skLineSegment(sketch, "E97.0", {"start": v(-17.47, -0.7) * mm, "end": v(-15.74, -3.7) * mm});
            skLineSegment(sketch, "E97.1", {"start": v(-15.74, -3.7) * mm, "end": v(-17.47, -6.7) * mm});
            skLineSegment(sketch, "E97.2", {"start": v(-17.47, -6.7) * mm, "end": v(-19, -6.7) * mm});
            skLineSegment(sketch, "E97.5", {"start": v(-19, -0.7) * mm, "end": v(-17.47, -0.7) * mm});
            skPoint(sketch, "E97.0.midPoint", {"position": v(-16.6, -2.2) * mm});
            skArc(sketch, "E98.cCircle", {"start": v(-19, -14.08) * mm, "mid": v(-16.2, -11.09) * mm, "end": v(-19, -8.1) * mm, "construction": true});
            skLineSegment(sketch, "E98.0", {"start": v(-19, -8.09) * mm, "end": v(-17.47, -8.09) * mm});
            skLineSegment(sketch, "E98.1", {"start": v(-17.47, -8.09) * mm, "end": v(-15.74, -11.09) * mm});
            skLineSegment(sketch, "E98.2", {"start": v(-15.74, -11.09) * mm, "end": v(-17.47, -14.09) * mm});
            skLineSegment(sketch, "E98.3", {"start": v(-17.47, -14.09) * mm, "end": v(-19, -14.09) * mm});
            skPoint(sketch, "E98.0.midPoint", {"position": v(-19.2, -8.09) * mm});
            skArc(sketch, "E99.cCircle", {"start": v(-16.32, -19.32) * mm, "mid": v(-16.74, -16.76) * mm, "end": v(-19, -15.48) * mm, "construction": true});
            skLineSegment(sketch, "E99.0", {"start": v(-19, -15.48) * mm, "end": v(-17.47, -15.48) * mm});
            skLineSegment(sketch, "E99.1", {"start": v(-17.47, -15.48) * mm, "end": v(-15.74, -18.48) * mm});
            skLineSegment(sketch, "E99.2", {"start": v(-15.74, -18.48) * mm, "end": v(-16.23, -19.32) * mm});
            skPoint(sketch, "E99.0.midPoint", {"position": v(-19.2, -15.48) * mm});
            skPoint(sketch, "E100.orphan", {"position": v(-17.47, 14.09) * mm});
            skPoint(sketch, "E101.trimOffspring.end.orphan", {"position": v(-20.93, 14.09) * mm});
            skArc(sketch, "E102.trimOffspring", {"start": v(-15.77, 13.93) * mm, "mid": v(-13.97, 15.4) * mm, "end": v(-13.3, 17.62) * mm});
            skLineSegment(sketch, "E103.trimOffspring", {"start": v(-19, 8.09) * mm, "end": v(-19, 13.62) * mm});
            skPoint(sketch, "E104.orphan", {"position": v(-20.93, -0.7) * mm});
            skPoint(sketch, "E105.orphan", {"position": v(-20.93, -8.09) * mm});
            skLineSegment(sketch, "E106.trimOffspring", {"start": v(-19, -6.7) * mm, "end": v(-19, -0.7) * mm});
            skPoint(sketch, "E107.trimOffspring.end.orphan", {"position": v(-20.93, -15.48) * mm});
            skLineSegment(sketch, "E108.trimOffspring", {"start": v(-19, -14.09) * mm, "end": v(-19, -8.09) * mm});
            skLineSegment(sketch, "E109.trimOffspring", {"start": v(-9.37, -19.32) * mm, "end": v(-3.43, -19.32) * mm});
            skLineSegment(sketch, "E110.trimOffspring", {"start": v(-19, 0.7) * mm, "end": v(-19, 6.7) * mm});
            skPoint(sketch, "E111.orphan", {"position": v(-8.13, -21.48) * mm});
            skLineSegment(sketch, "E112.trimOffspring", {"start": v(3.43, -19.32) * mm, "end": v(9.37, -19.32) * mm});
            skArc(sketch, "E113.cCircle", {"start": v(19, 6.69) * mm, "mid": v(16.2, 3.7) * mm, "end": v(19, 0.7) * mm, "construction": true});
            skLineSegment(sketch, "E113.0", {"start": v(17.47, 6.7) * mm, "end": v(19, 6.7) * mm});
            skLineSegment(sketch, "E113.3", {"start": v(19, 0.7) * mm, "end": v(17.47, 0.7) * mm});
            skLineSegment(sketch, "E113.4", {"start": v(17.47, 0.7) * mm, "end": v(15.74, 3.7) * mm});
            skLineSegment(sketch, "E113.5", {"start": v(15.74, 3.7) * mm, "end": v(17.47, 6.7) * mm});
            skPoint(sketch, "E113.0.midPoint", {"position": v(19.2, 6.7) * mm});
            skArc(sketch, "E114.cCircle", {"start": v(19, -0.7) * mm, "mid": v(16.2, -3.7) * mm, "end": v(19, -6.69) * mm, "construction": true});
            skLineSegment(sketch, "E114.0", {"start": v(17.47, -0.7) * mm, "end": v(19, -0.7) * mm});
            skLineSegment(sketch, "E114.4", {"start": v(17.47, -6.7) * mm, "end": v(15.74, -3.7) * mm});
            skLineSegment(sketch, "E114.5", {"start": v(15.74, -3.7) * mm, "end": v(17.47, -0.7) * mm});
            skPoint(sketch, "E114.0.midPoint", {"position": v(19.2, -0.7) * mm});
            skArc(sketch, "E115.cCircle", {"start": v(19, -8.1) * mm, "mid": v(16.2, -11.09) * mm, "end": v(19, -14.08) * mm, "construction": true});
            skLineSegment(sketch, "E115.0", {"start": v(17.47, -8.09) * mm, "end": v(19, -8.09) * mm});
            skLineSegment(sketch, "E115.3", {"start": v(19, -14.09) * mm, "end": v(17.47, -14.09) * mm});
            skLineSegment(sketch, "E115.4", {"start": v(17.47, -14.09) * mm, "end": v(15.74, -11.09) * mm});
            skLineSegment(sketch, "E115.5", {"start": v(15.74, -11.09) * mm, "end": v(17.47, -8.09) * mm});
            skPoint(sketch, "E115.0.midPoint", {"position": v(19.2, -8.09) * mm});
            skLineSegment(sketch, "E116.0", {"start": v(17.47, -15.48) * mm, "end": v(19, -15.48) * mm});
            skLineSegment(sketch, "E116.5", {"start": v(15.74, -18.48) * mm, "end": v(17.47, -15.48) * mm});
            skPoint(sketch, "E116.0.midPoint", {"position": v(19.2, -15.48) * mm});
            skPoint(sketch, "E113.1.start.orphan", {"position": v(20.93, 6.7) * mm});
            skLineSegment(sketch, "E117.trimOffspring", {"start": v(19, 8.09) * mm, "end": v(19, 13.62) * mm});
            skPoint(sketch, "E114.1.start.orphan", {"position": v(20.93, -0.7) * mm});
            skPoint(sketch, "E118.orphan", {"position": v(22.66, -3.7) * mm});
            skLineSegment(sketch, "E119.trimOffspring", {"start": v(19, -6.7) * mm, "end": v(17.47, -6.7) * mm});
            skLineSegment(sketch, "E120.trimOffspring", {"start": v(19, 0.7) * mm, "end": v(19, 6.7) * mm});
            skPoint(sketch, "E121.orphan", {"position": v(22.66, -11.09) * mm});
            skPoint(sketch, "E115.1.start.orphan", {"position": v(20.93, -8.09) * mm});
            skLineSegment(sketch, "E122.trimOffspring", {"start": v(16.23, -19.32) * mm, "end": v(15.74, -18.48) * mm});
            skArc(sketch, "E123.trimOffspring", {"start": v(19, -15.48) * mm, "mid": v(16.74, -16.76) * mm, "end": v(16.32, -19.32) * mm, "construction": true});
            skPoint(sketch, "E116.1.start.orphan", {"position": v(20.93, -15.48) * mm});
            skLineSegment(sketch, "E124.trimOffspring", {"start": v(16.23, -19.32) * mm, "end": v(19, -19.32) * mm});
            skLineSegment(sketch, "E125.trimOffspring", {"start": v(19, -14.09) * mm, "end": v(19, -8.09) * mm});
            skLineSegment(sketch, "E126.trimOffspring", {"start": v(19, -6.7) * mm, "end": v(19, -0.7) * mm});
            skSolve(sketch);
        }
        {
            var Q0;
            Q0=qSketchRegion(id+"F1",true);
            extrude(context, id + "F2", {"entities" : qUnion([Q0]), "depth" : 2 * mm, "offsetDistance" : 25 * mm});
        }
        {
            var Q0;
            Q0=makeQuery(id+"F2.opExtrude","CAP_EDGE",EDGE,{"disambiguationData":[OSD([sQuery(id+"F1.wireOp",EDGE,"E17")])],"isStart":false});
            var Q1;
            Q1=makeQuery(id+"F2.opExtrude","CAP_EDGE",EDGE,{"disambiguationData":[OSD([sQuery(id+"F1.wireOp",EDGE,"E24")])],"isStart":false});
            chamfer(context, id + "F3", {"entities" : qUnion([Q0, Q1]), "width" : 1 * mm, "tangentPropagation" : true});
        }
    });
